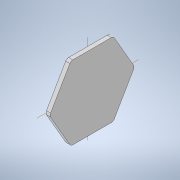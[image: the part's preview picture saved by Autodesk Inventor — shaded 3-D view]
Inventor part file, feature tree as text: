
AUTODESK INVENTOR PART (.ipt)
format: ipt  version: 2021.1 (Build 251245000, 245)  size: 113,664 bytes
history: native  units: in
note: dims shown in document units (in); Inventor stores cm internally (conversion verified against a paired STEP export)
features: extrude x1, sketch x1
ambient origin geometry x8: Origin, YZ Plane, XZ Plane, XY Plane, X Axis, Y Axis, Z Axis, Center Point
bodies: Solid1 (feature_tree)
feature tree (2):
  extrude  "Extrusion1"  Depth=0.5in
  sketch  "Sketch1"  dims[d0=10.6in d1=0.5in d2=0.6in d3=0.0in]
